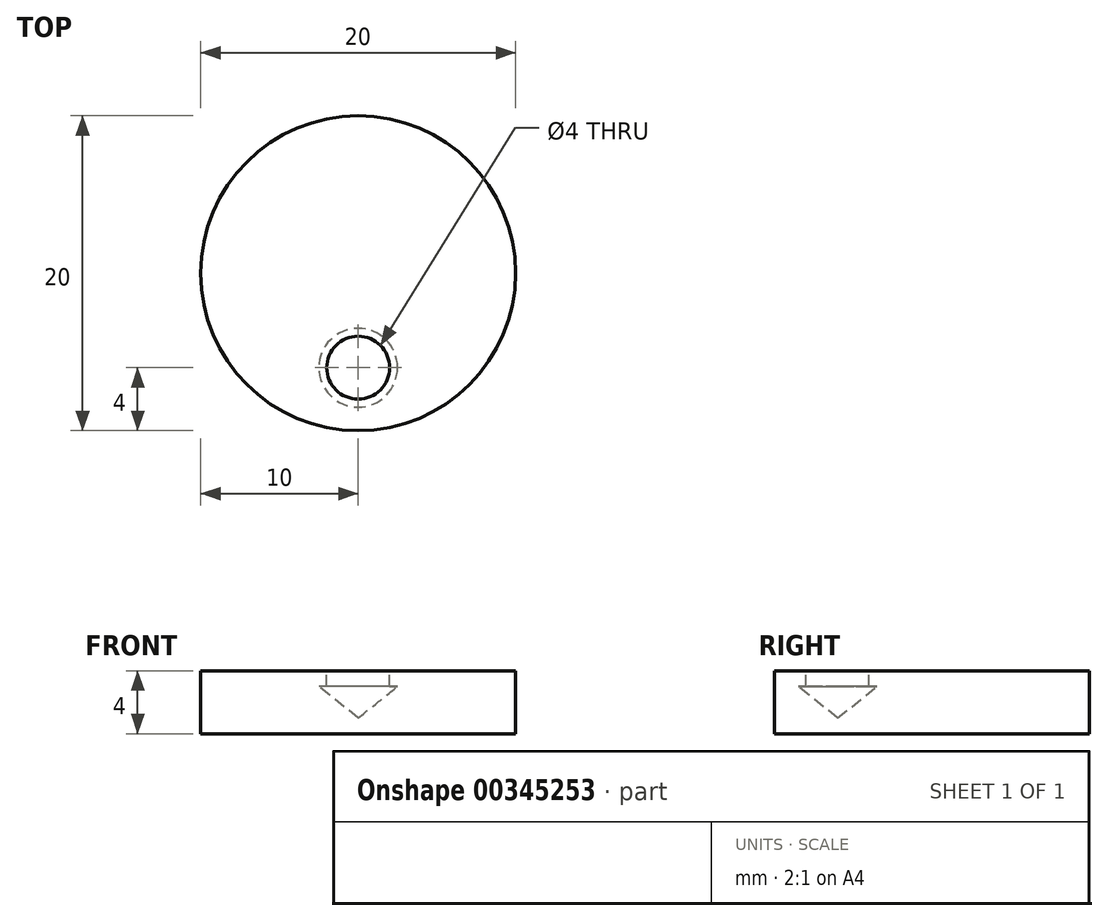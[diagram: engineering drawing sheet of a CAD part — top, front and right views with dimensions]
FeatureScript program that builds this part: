
annotation { "Feature Type Name" : "Feature", "Feature Type Description" : "" }
export const myFeature = defineFeature(function(context is Context, id is Id, definition is map)
    precondition{}
    {
        {
            var Q0;
            Q0=qCreatedBy(makeId("Top.planeOp"),FACE);
            var sketch = newSketch(context, id + "F0", { "sketchPlane" : qUnion([Q0])});
            skCircle(sketch, "E0", {"center": v(0, 0) * mm, "radius": 10 * mm});
            skSolve(sketch);
        }
        {
            var Q0;
            Q0=makeQuery(id+"F0.imprint","IMPRINT",FACE,{"disambiguationData":[TD([[makeQuery(id+"F0.imprint","IMPRINT",EDGE,{"derivedFrom":sQuery(id+"F0.wireOp",EDGE,"E0")}),1.0]])]});
            extrude(context, id + "F1", {"entities" : qUnion([Q0]), "depth" : 4 * mm});
        }
        {
            var Q0;
            Q0=makeQuery(id+"F1.opExtrude","CAP_FACE",FACE,{"disambiguationData":[OSD([sQuery(id+"F0.wireOp",EDGE,"E0")])],"isStart":false});
            var sketch = newSketch(context, id + "F2", { "sketchPlane" : qUnion([Q0])});
            skCircle(sketch, "E1", {"center": v(0, -6) * mm, "radius": 2 * mm});
            skSolve(sketch);
        }
        {
            var Q0;
            Q0 = qSketchRegion(id + "F2", true);
            extrude(context, id + "F3", {"entities" : qUnion([Q0]), "operationType" : NewBodyOperationType.REMOVE, "oppositeDirection" : true, "depth" : 1 * mm});
        }
        {
            var Q0;
            Q0=qCreatedBy(makeId("Front.planeOp"),FACE);
            cPlane(context, id + "F4", {"entities" : qUnion([Q0]), "cplaneType" : CPlaneType.OFFSET, "offset" : 6 * mm, "width" : 150 * mm, "height" : 150 * mm});
        }
        {
            var Q0;
            Q0=qCreatedBy(id+"F4.planeOp",FACE);
            var sketch = newSketch(context, id + "F5", { "sketchPlane" : qUnion([Q0])});
            skLineSegment(sketch, "E2.0", {"start": v(-2, 3) * mm, "end": v(2, 3) * mm, "construction": true});
            skLineSegment(sketch, "E3", {"start": v(0, 1) * mm, "end": v(0, 3) * mm});
            skLineSegment(sketch, "E4", {"start": v(0, 3) * mm, "end": v(2.5, 3) * mm});
            skLineSegment(sketch, "E5", {"start": v(0, 1) * mm, "end": v(2.5, 3) * mm});
            skSolve(sketch);
        }
        {
            var Q0;
            Q0 = qSketchRegion(id + "F5", true);
            var Q1;
            Q1=sQuery(id+"F5.wireOp",EDGE,"E3");
            revolve(context, id + "F6", {"operationType" : NewBodyOperationType.REMOVE, "entities" : qUnion([Q0]), "axis" : qUnion([Q1]), "revolveType" : RevolveType.FULL, "oppositeDirection" : true});
        }
    });
